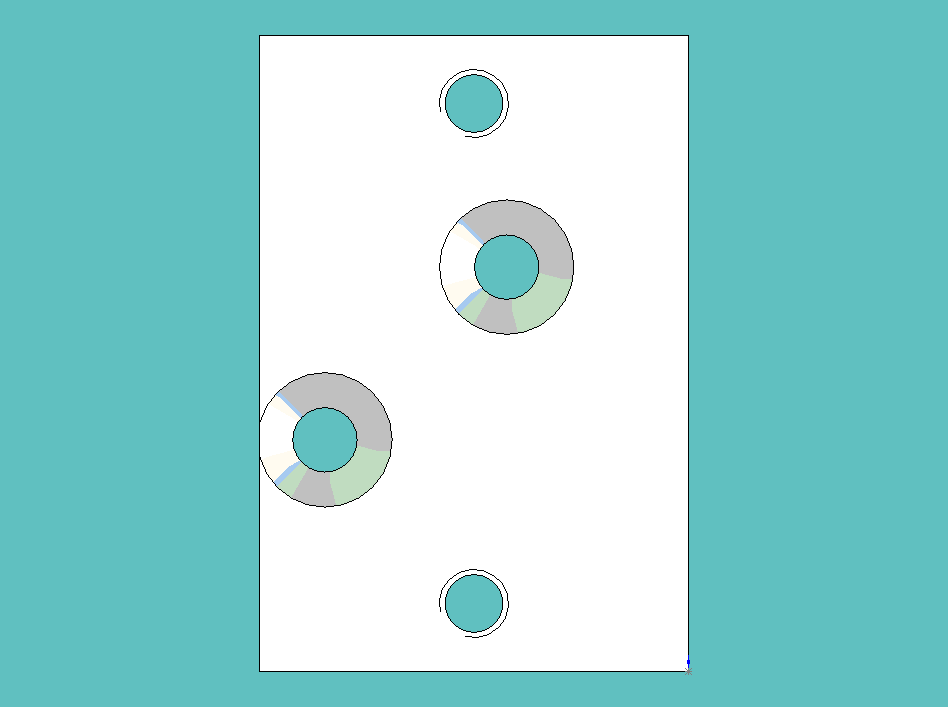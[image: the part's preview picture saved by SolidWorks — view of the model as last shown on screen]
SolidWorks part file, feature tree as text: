
SOLIDWORKS PART (.sldprt)
format: sldprt  version: not decoded by parser v0  size: 206,848 bytes
history: native  units: mm
features: sketch x5, hole x2, thread x2, material x1, extrude x1 (+13 scaffold rows collapsed)
feature tree (24):
  scaffold x13  (default folders/planes/origin — collapsed)
  material  "Material <not specified>"
  sketch  "Sketch1"  dims[D1=44.45mm D2=29.972mm D3=17.4625mm D4=17.4625mm]
  extrude  "Extrude1"  Depth=4.7625mm
  hole  "#10-32 Tapped Hole1"  Diameter=4.0386mm Depth=4.7625mm
  sketch  "Sketch9"  dims[D1=4.7625mm D2=14.986mm D3=34.925mm]
  sketch  "Sketch8"  dims[hole-wizard template sketch: 60 standard entries collapsed; hole parameters kept: c18.Thru Tap Drill Depth=4.7625mm]
  thread  "Cosmetic Thread3"  Diameter=4.826mm  [1 undecoded]
  thread  "Cosmetic Thread4"  Diameter=4.826mm  [1 undecoded]
  hole  "CSK for M4 Flat Head Machine Screw1"  Diameter=4.5mm Depth=4.7625mm
  sketch  "Sketch11"  dims[D1=25.4mm D2=12.7mm D3=16.1925mm D4=16.1925mm D5=12.065mm]
  sketch  "Sketch10"  dims[hole-wizard template sketch: 55 standard entries collapsed; hole parameters kept: c17.Thru Hole Depth=4.7625mm c17.Near C'Sink Dia.=9.4mm c17.D4=~3.666174mm c17.Near C'Sink Angle=90.0deg]
decode coverage: 10 of 10 modeling features carry decoded parameters
note: ~ marks probable driven/reference dimensions
note: 2 parameter values undecoded
note: suppression state not decoded; provenance and decode notes live in map.json
